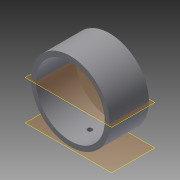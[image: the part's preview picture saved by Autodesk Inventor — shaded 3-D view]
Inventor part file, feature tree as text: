
AUTODESK INVENTOR PART (.ipt)
format: ipt  version: 2014 SP1 (Build 180222100, 222)  size: 94,720 bytes
history: native  units: in
note: dims shown in document units (in); Inventor stores cm internally (conversion verified against a paired STEP export)
features: extrude x2, sketch x2, plane x1
ambient origin geometry x8: Origin, YZ Plane, XZ Plane, XY Plane, X Axis, Y Axis, Z Axis, Center Point
bodies: Solid1 (feature_tree)
feature tree (5):
  extrude  "Extrusion1"  Depth=0.125in
  plane  "Work Plane1"
  extrude  "Extrusion2"  Depth=1.0in
  sketch  "Sketch1"  dims[d2=2.0in d3=0.125in]
  sketch  "Sketch2"  dims[d4=1.0in d5=0.0in d6=0.125in d7=0.5in d8=1.0in d9=0.0in]
